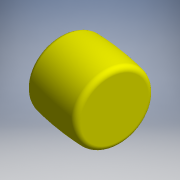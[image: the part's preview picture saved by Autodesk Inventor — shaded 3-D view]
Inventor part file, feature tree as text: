
AUTODESK INVENTOR PART (.ipt)
format: ipt  version: 2017.3 (Build 213256000, 256)  size: 130,560 bytes
history: native  units: mm (DEFAULTED — no unit token found)
features: other x14, revolve x1, sketch x1
ambient origin geometry x8: Origin, YZ Plane, XZ Plane, XY Plane, X Axis, Y Axis, Z Axis, Center Point
bodies: Solid1 (feature_tree)
feature tree (16):
  revolve  "Revolution1"  [1 undecoded]
  other  "NO_GEO_XY"
  other  "NO_GEO_YZ"
  other  "NO_GEO_ZX"
  other  "NO_GEO_X"
  other  "NO_GEO_Y"
  other  "NO_GEO_Z"
  other  "NO_GEO_Center"
  other  "roller1_XY"
  other  "roller1_YZ"
  other  "roller1_ZX"
  other  "roller1_X"
  other  "roller1_Y"
  other  "roller1_Z"
  other  "roller1_Center"
  sketch  "Sketch_2"  dims[d0=360.0deg]
note: 1 required parameter value undecoded (feature->parameter linkage not recoverable at this tier; creation-order binding heuristic only, values carry confidence <= 0.55)
